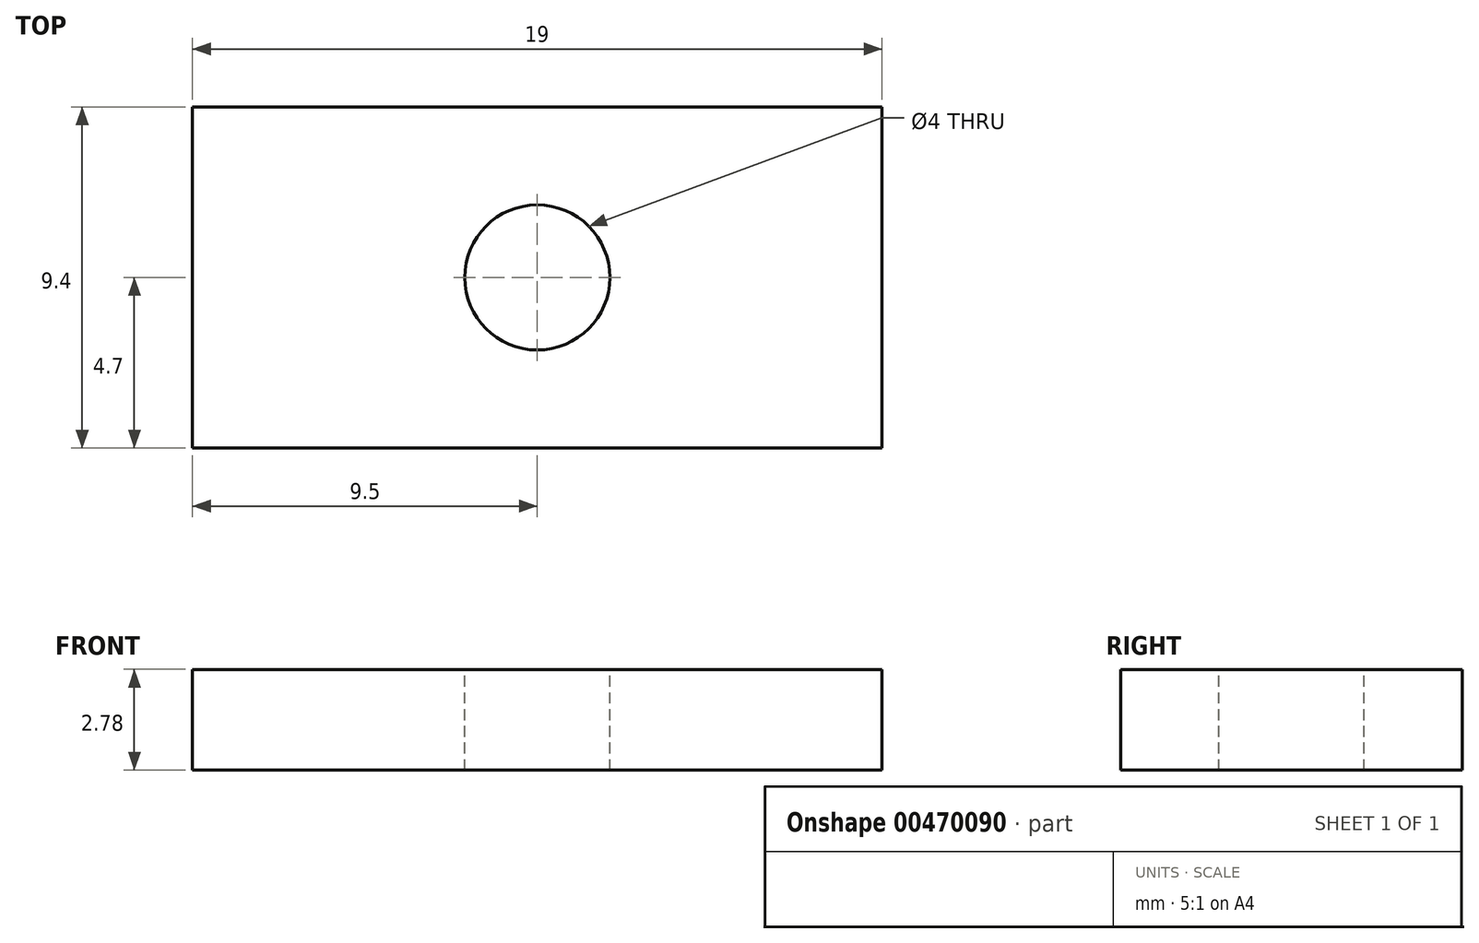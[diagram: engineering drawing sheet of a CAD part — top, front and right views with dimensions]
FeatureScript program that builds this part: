
annotation { "Feature Type Name" : "Feature", "Feature Type Description" : "" }
export const myFeature = defineFeature(function(context is Context, id is Id, definition is map)
    precondition{}
    {
        {
            var Q0;
            Q0=qCreatedBy(makeId("Top.planeOp"),FACE);
            var sketch = newSketch(context, id + "F0", { "sketchPlane" : qUnion([Q0])});
            skLineSegment(sketch, "E0.bottom", {"start": v(0, 0) * mm, "end": v(19, 0) * mm});
            skLineSegment(sketch, "E0.top", {"start": v(0, -9.4) * mm, "end": v(19, -9.4) * mm});
            skLineSegment(sketch, "E0.left", {"start": v(0, 0) * mm, "end": v(0, -9.4) * mm});
            skLineSegment(sketch, "E0.right", {"start": v(19, 0) * mm, "end": v(19, -9.4) * mm});
            skSolve(sketch);
        }
        {
            var Q0;
            Q0=makeQuery(id+"F0.imprint","IMPRINT",FACE,{"disambiguationData":[TD([[makeQuery(id+"F0.imprint","IMPRINT",EDGE,{"derivedFrom":sQuery(id+"F0.wireOp",EDGE,"E0.bottom")}),-1.0]])]});
            extrude(context, id + "F1", {"entities" : qUnion([Q0]), "depth" : 2.77 * mm});
        }
        {
            var Q0;
            Q0=makeQuery(id+"F1.opExtrude","CAP_FACE",FACE,{"disambiguationData":[OSD([sQuery(id+"F0.wireOp",EDGE,"E0.bottom"),sQuery(id+"F0.wireOp",EDGE,"E0.top"),sQuery(id+"F0.wireOp",EDGE,"E0.left"),sQuery(id+"F0.wireOp",EDGE,"E0.right")])],"isStart":false});
            var sketch = newSketch(context, id + "F2", { "sketchPlane" : qUnion([Q0])});
            skLineSegment(sketch, "E1", {"start": v(9.5, 0) * mm, "end": v(9.5, -9.4) * mm, "construction": true});
            skLineSegment(sketch, "E2", {"start": v(19, -4.7) * mm, "end": v(0, -4.7) * mm, "construction": true});
            skCircle(sketch, "E3", {"center": v(9.5, -4.7) * mm, "radius": 2 * mm});
            skSolve(sketch);
        }
        {
            var Q0;
            Q0=makeQuery(id+"F2.imprint","IMPRINT",FACE,{"disambiguationData":[TD([[makeQuery(id+"F2.imprint","IMPRINT",EDGE,{"derivedFrom":sQuery(id+"F2.wireOp",EDGE,"E3")}),1.0]])]});
            extrude(context, id + "F3", {"entities" : qUnion([Q0]), "operationType" : NewBodyOperationType.REMOVE, "oppositeDirection" : true, "depth" : 25 * mm});
        }
    });
